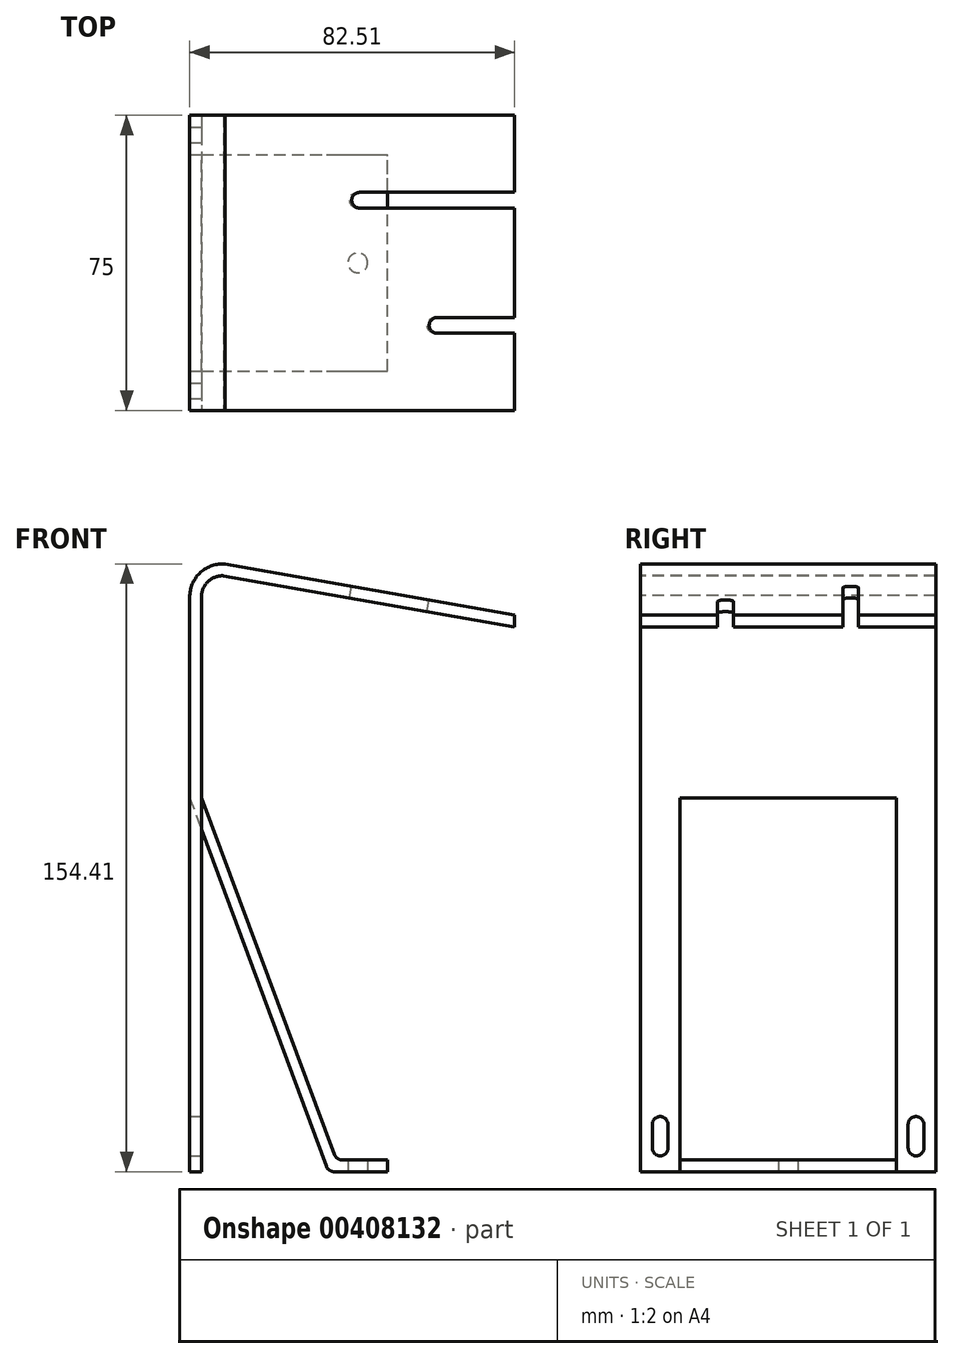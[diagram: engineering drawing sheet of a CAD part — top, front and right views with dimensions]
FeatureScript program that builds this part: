
annotation { "Feature Type Name" : "Feature", "Feature Type Description" : "" }
export const myFeature = defineFeature(function(context is Context, id is Id, definition is map)
    precondition{}
    {
        {
            var Q0;
            Q0=qCreatedBy(makeId("Front.planeOp"),FACE);
            var sketch = newSketch(context, id + "F0", { "sketchPlane" : qUnion([Q0])});
            skLineSegment(sketch, "E0", {"start": v(0, 0) * mm, "end": v(0, 146.33) * mm});
            skLineSegment(sketch, "E1", {"start": v(5.65, 151.4) * mm, "end": v(79.5, 138.37) * mm});
            skArc(sketch, "E2", {"start": v(5.65, 151.4) * mm, "mid": v(1.77, 150.04) * mm, "end": v(0, 146.33) * mm});
            skLineSegment(sketch, "E3.0", {"start": v(-3, 0) * mm, "end": v(-3, 146.2) * mm});
            skLineSegment(sketch, "E4.0", {"start": v(-3, 0) * mm, "end": v(-3, 146.4) * mm});
            skArc(sketch, "E4.1", {"start": v(6.01, 154.38) * mm, "mid": v(-0.2, 152.3) * mm, "end": v(-3, 146.4) * mm});
            skLineSegment(sketch, "E4.2", {"start": v(6.01, 154.38) * mm, "end": v(79.5, 141.42) * mm});
            skLineSegment(sketch, "E5", {"start": v(0, 0) * mm, "end": v(-3, 0) * mm});
            skLineSegment(sketch, "E6", {"start": v(79.5, 138.37) * mm, "end": v(79.5, 141.42) * mm});
            skSolve(sketch);
        }
        {
            var Q0;
            Q0 = qSketchRegion(id + "F0", true);
            extrude(context, id + "F1", {"entities" : qUnion([Q0]), "oppositeDirection" : true, "depth" : 75 * mm});
        }
        {
            var Q0;
            Q0=makeQuery(id+"F1.opExtrude","SWEPT_FACE",FACE,{"disambiguationData":[OSD([sQuery(id+"F0.wireOp",EDGE,"E0")])]});
            var sketch = newSketch(context, id + "F2", { "sketchPlane" : qUnion([Q0])});
            skLineSegment(sketch, "E7.bottom", {"start": v(10, 0) * mm, "end": v(65, 0) * mm});
            skLineSegment(sketch, "E7.top", {"start": v(10, 95) * mm, "end": v(65, 95) * mm});
            skLineSegment(sketch, "E7.left", {"start": v(10, 0) * mm, "end": v(10, 95) * mm});
            skLineSegment(sketch, "E7.right", {"start": v(65, 0) * mm, "end": v(65, 95) * mm});
            skSolve(sketch);
        }
        {
            var Q0;
            Q0=makeQuery(id+"F2.imprint","IMPRINT",FACE,{"disambiguationData":[TD([[makeQuery(id+"F2.imprint","IMPRINT",EDGE,{"derivedFrom":sQuery(id+"F2.wireOp",EDGE,"E7.bottom")}),-1.0]])]});
            extrude(context, id + "F3", {"entities" : qUnion([Q0]), "operationType" : NewBodyOperationType.REMOVE, "endBound" : BoundingType.THROUGH_ALL, "oppositeDirection" : true, "depth" : 25 * mm});
        }
        {
            var Q0;
            Q0=makeQuery(id+"F3.boolean.opBoolean","COPY",FACE,{"derivedFrom":makeQuery(id+"F3.opExtrude","SWEPT_FACE",FACE,{"disambiguationData":[OSD([sQuery(id+"F2.wireOp",EDGE,"E7.right")])]})});
            var sketch = newSketch(context, id + "F4", { "sketchPlane" : qUnion([Q0])});
            skLineSegment(sketch, "E8", {"start": v(-3, 95) * mm, "end": v(32.2, 0) * mm});
            skLineSegment(sketch, "E9", {"start": v(32.2, 0) * mm, "end": v(47.2, 0) * mm});
            skLineSegment(sketch, "E10.0", {"start": v(34.3, 3) * mm, "end": v(47.2, 3) * mm});
            skLineSegment(sketch, "E11", {"start": v(47.2, 0) * mm, "end": v(47.2, 3) * mm});
            skLineSegment(sketch, "E12", {"start": v(-3, 95) * mm, "end": v(0, 95) * mm});
            skLineSegment(sketch, "E13", {"start": v(0, 95) * mm, "end": v(34.3, 3) * mm});
            skSolve(sketch);
        }
        {
            var Q0;
            Q0 = qSketchRegion(id + "F4", true);
            extrude(context, id + "F5", {"entities" : qUnion([Q0]), "operationType" : NewBodyOperationType.ADD, "depth" : 55 * mm});
        }
        {
            var Q0;
            Q0=makeQuery(id+"F5.opExtrude","SWEPT_FACE",FACE,{"disambiguationData":[OSD([sQuery(id+"F4.wireOp",EDGE,"E9")])]});
            var sketch = newSketch(context, id + "F6", { "sketchPlane" : qUnion([Q0])});
            skLineSegment(sketch, "E14", {"start": v(39.7, -10) * mm, "end": v(39.7, -65) * mm});
            skCircle(sketch, "E15", {"center": v(39.7, -37.5) * mm, "radius": 2.5 * mm});
            skSolve(sketch);
        }
        {
            var Q0;
            Q0 = qSketchRegion(id + "F6", true);
            extrude(context, id + "F7", {"entities" : qUnion([Q0]), "operationType" : NewBodyOperationType.REMOVE, "oppositeDirection" : true, "depth" : 3 * mm});
        }
        {
            var Q0;
            Q0=makeQuery(id+"F1.opExtrude","SWEPT_FACE",FACE,{"disambiguationData":[OSD([sQuery(id+"F0.wireOp",EDGE,"E0")])]});
            var sketch = newSketch(context, id + "F8", { "sketchPlane" : qUnion([Q0])});
            skLineSegment(sketch, "E16", {"start": v(7, 12) * mm, "end": v(7, 6) * mm});
            skLineSegment(sketch, "E17", {"start": v(3, 12) * mm, "end": v(3, 6) * mm});
            skLineSegment(sketch, "E18", {"start": v(68, 12) * mm, "end": v(68, 6) * mm});
            skLineSegment(sketch, "E19", {"start": v(72, 12) * mm, "end": v(72, 6) * mm});
            skArc(sketch, "E20", {"start": v(7, 12) * mm, "mid": v(5, 14) * mm, "end": v(3, 12) * mm});
            skArc(sketch, "E21", {"start": v(3, 6) * mm, "mid": v(5, 4) * mm, "end": v(7, 6) * mm});
            skArc(sketch, "E22", {"start": v(72, 12) * mm, "mid": v(70, 14) * mm, "end": v(68, 12) * mm});
            skArc(sketch, "E23", {"start": v(68, 6) * mm, "mid": v(70, 4) * mm, "end": v(72, 6) * mm});
            skSolve(sketch);
        }
        {
            var Q0;
            Q0 = qSketchRegion(id + "F8", true);
            extrude(context, id + "F9", {"entities" : qUnion([Q0]), "operationType" : NewBodyOperationType.REMOVE, "endBound" : BoundingType.UP_TO_NEXT, "oppositeDirection" : true, "depth" : 25 * mm});
        }
        {
            var Q0;
            Q0=makeQuery(id+"F5.opExtrude","SWEPT_EDGE",EDGE,{"disambiguationData":[OSD([sQuery(id+"F4.wireOp",EDGE,"E8"),sQuery(id+"F4.wireOp",EDGE,"E9")])]});
            var Q1;
            Q1=makeQuery(id+"F5.opExtrude","SWEPT_EDGE",EDGE,{"disambiguationData":[OSD([sQuery(id+"F4.wireOp",EDGE,"E10.0"),sQuery(id+"F4.wireOp",EDGE,"E13")])]});
            fillet(context, id + "F10", {"entities" : qUnion([Q0, Q1]), "radius" : 2 * mm, "tangentPropagation" : true, "allowEdgeOverflow" : false});
        }
        {
            var Q0;
            Q0=makeQuery(id+"F1.opExtrude","SWEPT_FACE",FACE,{"disambiguationData":[OSD([sQuery(id+"F0.wireOp",EDGE,"E4.2")])]});
            var sketch = newSketch(context, id + "F11", { "sketchPlane" : qUnion([Q0])});
            skArc(sketch, "E24", {"start": v(33.74, 23.6) * mm, "mid": v(31.74, 21.6) * mm, "end": v(33.74, 19.6) * mm});
            skArc(sketch, "E25", {"start": v(13.74, 55.4) * mm, "mid": v(11.74, 53.4) * mm, "end": v(13.74, 51.4) * mm});
            skLineSegment(sketch, "E26", {"start": v(13.74, 55.4) * mm, "end": v(53.74, 55.4) * mm});
            skLineSegment(sketch, "E27", {"start": v(13.74, 51.4) * mm, "end": v(53.74, 51.4) * mm});
            skLineSegment(sketch, "E28", {"start": v(33.74, 23.6) * mm, "end": v(53.74, 23.6) * mm});
            skLineSegment(sketch, "E29", {"start": v(33.74, 19.6) * mm, "end": v(53.74, 19.6) * mm});
            skLineSegment(sketch, "E30", {"start": v(53.74, 19.6) * mm, "end": v(53.74, 23.6) * mm});
            skLineSegment(sketch, "E31.trimOffspring", {"start": v(53.74, 51.4) * mm, "end": v(53.74, 55.4) * mm});
            skLineSegment(sketch, "E32", {"start": v(33.74, 21.6) * mm, "end": v(33.74, 53.4) * mm});
            skLineSegment(sketch, "E33", {"start": v(53.74, 37.5) * mm, "end": v(-20.89, 37.5) * mm});
            skSolve(sketch);
        }
        {
            var Q0;
            Q0 = qSketchRegion(id + "F11", true);
            extrude(context, id + "F12", {"entities" : qUnion([Q0]), "operationType" : NewBodyOperationType.REMOVE, "endBound" : BoundingType.UP_TO_NEXT, "oppositeDirection" : true, "depth" : 4 * mm});
        }
        {
            var Q0;
            Q0=makeQuery(id+"F1.opExtrude","SWEPT_FACE",FACE,{"disambiguationData":[OSD([sQuery(id+"F0.wireOp",EDGE,"E6")])]});
            var sketch = newSketch(context, id + "F13", { "sketchPlane" : qUnion([Q0])});
            skLineSegment(sketch, "E34.bottom", {"start": v(19.6, 141.42) * mm, "end": v(23.6, 141.42) * mm});
            skLineSegment(sketch, "E34.top", {"start": v(19.6, 138.37) * mm, "end": v(23.6, 138.37) * mm});
            skLineSegment(sketch, "E34.left", {"start": v(19.6, 141.42) * mm, "end": v(19.6, 138.37) * mm});
            skLineSegment(sketch, "E34.right", {"start": v(23.6, 141.42) * mm, "end": v(23.6, 138.37) * mm});
            skLineSegment(sketch, "E35.bottom", {"start": v(51.4, 141.42) * mm, "end": v(55.4, 141.42) * mm});
            skLineSegment(sketch, "E35.top", {"start": v(51.4, 138.37) * mm, "end": v(55.4, 138.37) * mm});
            skLineSegment(sketch, "E35.left", {"start": v(51.4, 141.42) * mm, "end": v(51.4, 138.37) * mm});
            skLineSegment(sketch, "E35.right", {"start": v(55.4, 141.42) * mm, "end": v(55.4, 138.37) * mm});
            skSolve(sketch);
        }
        {
            var Q0;
            Q0 = qSketchRegion(id + "F13", true);
            extrude(context, id + "F14", {"entities" : qUnion([Q0]), "operationType" : NewBodyOperationType.REMOVE, "oppositeDirection" : true, "depth" : 1 * mm});
        }
    });
